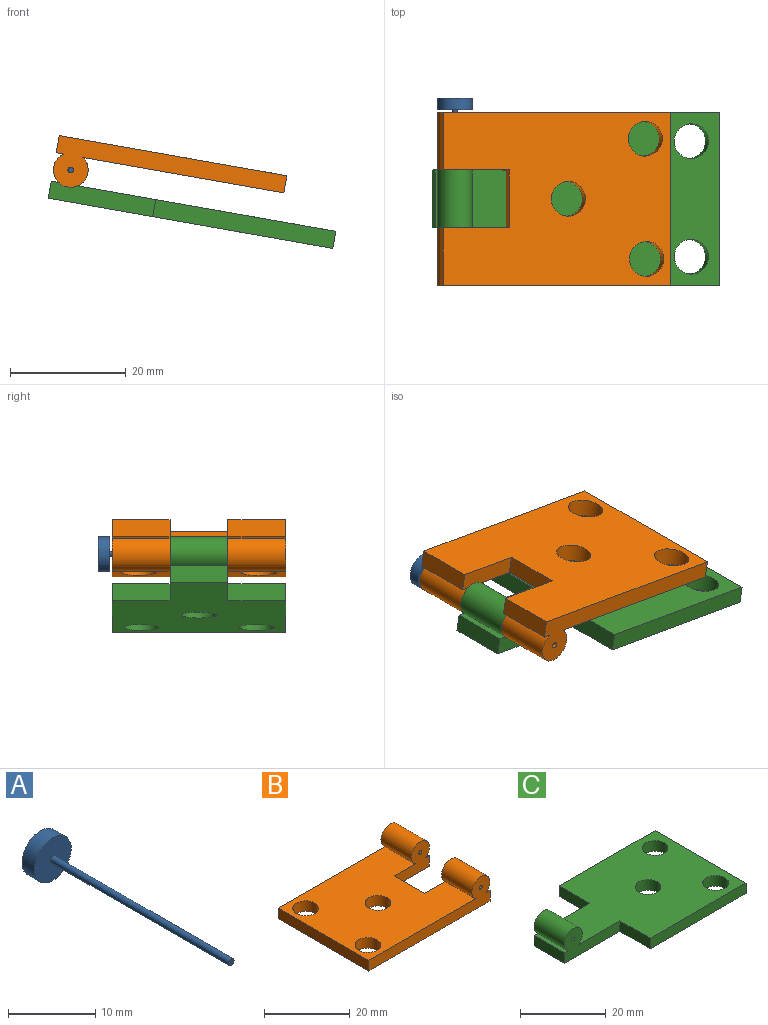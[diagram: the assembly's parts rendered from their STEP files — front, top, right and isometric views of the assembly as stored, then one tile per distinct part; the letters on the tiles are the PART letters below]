
ASSEMBLY  parts=3 mates=3
PART A: 5 faces, bbox 6x31x6 mm
  f0: cylinder r=0.45mm len=29mm, axis (0,1,0), area 82mm2, adj f1,f3
  f1: plane 0.9x0.9mm, normal (0,-1,0), area 0.6mm2, adj f0
  f2: cylinder r=3mm len=6mm, axis (0,1,0), area 37.7mm2, adj f3,f4
  f3: plane 6x6mm, normal (0,-1,0), area 27.6mm2, adj f0,f2
  f4: plane 6x6mm, normal (0,1,0), area 28.3mm2, adj f2
PART B: 19 faces, bbox 40x30x8.5 mm
  f0: plane 10x1.34mm, normal (0,0,1), area 13.4mm2, adj f7,f8,f11,f18
  f1: plane 35.34x30mm, normal (0,0,1), area 905.8mm2, adj f2,f3,f5,f6,f7,f9,f10,f11
  f2: plane 30x3mm, normal (-1,0,0), area 90mm2, adj f1,f3,f11,f14
  f3: plane 40x8.5mm, normal (0,-1,0), area 146.4mm2, adj f1,f2,f4,f13,f14,f15,f16
  f4: plane 10x3mm, normal (1,0,0), area 30mm2, adj f3,f5,f13,f14
  f5: plane 11.62x8.5mm, normal (0,1,0), area 61.2mm2, adj f1,f4,f6,f13,f14,f15,f16
  f6: plane 10x3mm, normal (1,0,0), area 30mm2, adj f1,f5,f7,f14
  f7: plane 11.62x8.5mm, normal (0,-1,0), area 61.2mm2, adj f0,f1,f6,f8,f14,f17,f18
  f8: plane 10x3mm, normal (1,0,0), area 30mm2, adj f0,f7,f11,f14
  f9: cylinder r=3mm len=6mm, axis (0,0,-1), area 56.5mm2, adj f1,f14
  f10: cylinder r=3mm len=6mm, axis (0,0,-1), area 56.5mm2, adj f1,f14
  f11: plane 40x8.5mm, normal (0,1,0), area 146.4mm2, adj f0,f1,f2,f8,f14,f17,f18
  f12: cylinder r=3mm len=6mm, axis (0,0,-1), area 56.5mm2, adj f1,f14
  f13: plane 10x1.34mm, normal (0,0,1), area 13.4mm2, adj f3,f4,f5,f16
  f14: plane 40x30mm, normal (0,0,-1), area 999mm2, adj f2,f3,f4,f5,f6,f7,f8,f9
  f15: cylinder r=0.5mm len=10mm, axis (0,-1,0), area 31.4mm2, adj f3,f5
  f16: cylinder r=3mm len=10mm, axis (0,-1,0), area 153.4mm2, adj f1,f3,f5,f13
  f17: cylinder r=0.5mm len=10mm, axis (0,1,0), area 31.4mm2, adj f7,f11
  f18: cylinder r=3mm len=10mm, axis (0,1,0), area 153.4mm2, adj f0,f1,f7,f11
PART C: 16 faces, bbox 50x30x8.5 mm
  f0: plane 10x1.34mm, normal (0,0,1), area 13.4mm2, adj f1,f7,f10,f14
  f1: plane 18.37x8.5mm, normal (0,-1,0), area 81.5mm2, adj f0,f2,f10,f12,f13,f14,f15
  f2: plane 10x3mm, normal (-1,0,0), area 30mm2, adj f1,f3,f12,f13
  f3: plane 31.63x3mm, normal (0,-1,0), area 94.9mm2, adj f2,f4,f12,f13
  f4: plane 30x3mm, normal (1,0,0), area 90mm2, adj f3,f5,f12,f13
  f5: plane 31.63x3mm, normal (0,1,0), area 94.9mm2, adj f4,f6,f12,f13
  f6: plane 10x3mm, normal (-1,0,0), area 30mm2, adj f5,f7,f12,f13
  f7: plane 18.37x8.5mm, normal (0,1,0), area 81.5mm2, adj f0,f6,f10,f12,f13,f14,f15
  f8: cylinder r=3mm len=6mm, axis (0,0,-1), area 56.5mm2, adj f12,f13
  f9: cylinder r=3mm len=6mm, axis (0,0,-1), area 56.5mm2, adj f12,f13
  f10: plane 10x3mm, normal (-1,0,0), area 30mm2, adj f0,f1,f7,f13
  f11: cylinder r=3mm len=6mm, axis (0,0,-1), area 56.5mm2, adj f12,f13
  f12: plane 45.34x30mm, normal (0,0,1), area 1001.3mm2, adj f1,f2,f3,f4,f5,f6,f7,f8
  f13: plane 50x30mm, normal (0,0,-1), area 1047.9mm2, adj f1,f2,f3,f4,f5,f6,f7,f8
  f14: cylinder r=3mm len=10mm, axis (0,-1,0), area 153.4mm2, adj f0,f1,f7,f12
  f15: cylinder r=0.5mm len=10mm, axis (0,-1,0), area 31.4mm2, adj f1,f7
PLACE A rot(axis=(0,1,0),10deg) t=(-21.88,47.53,40.43)mm
PLACE B rot(axis=(0,-1,0),170deg) t=(-23.88,15.14,46.37)mm
PLACE C rot(axis=(0,1,0),10deg) t=(-1.38,40.14,31.23)mm fixed
MATE revolute B.f15 <-> C.f14  axis (0,1,0) through (-21.88,35.14,40.43)mm
MATE slider A.f0 <-> C.f14  axis (0,1,0) through (-21.88,31.03,40.43)mm
MATE planar C.f14 <-> B.f15  axis (0,-1,0) through (-21.88,35.14,40.43)mm
